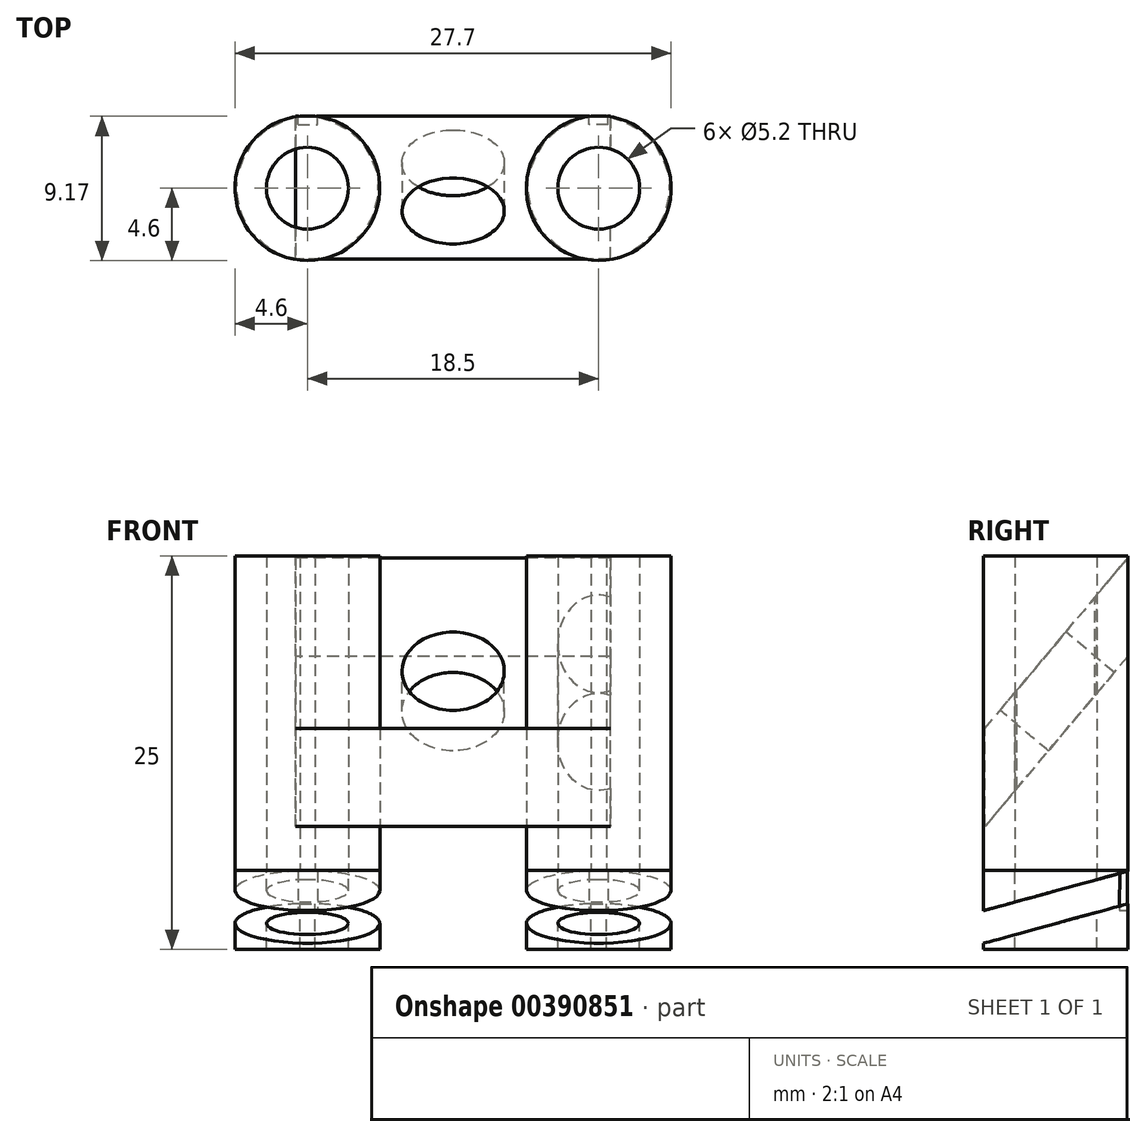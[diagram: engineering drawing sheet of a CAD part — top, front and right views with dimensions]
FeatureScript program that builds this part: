
annotation { "Feature Type Name" : "Feature", "Feature Type Description" : "" }
export const myFeature = defineFeature(function(context is Context, id is Id, definition is map)
    precondition{}
    {
        {
            var Q0;
            Q0=qCreatedBy(makeId("Top.planeOp"),FACE);
            var sketch = newSketch(context, id + "F0", { "sketchPlane" : qUnion([Q0])});
            skCircle(sketch, "E0", {"center": v(-9.25, 0) * mm, "radius": 2.6 * mm});
            skCircle(sketch, "E1", {"center": v(9.25, 0) * mm, "radius": 2.6 * mm});
            skCircle(sketch, "E2", {"center": v(-9.25, 0) * mm, "radius": 4.6 * mm});
            skCircle(sketch, "E3", {"center": v(9.25, 0) * mm, "radius": 4.6 * mm});
            skSolve(sketch);
        }
        {
            var Q0;
            Q0=makeQuery(id+"F0.imprint","IMPRINT",FACE,{"disambiguationData":[TD([[makeQuery(id+"F0.imprint","IMPRINT",EDGE,{"derivedFrom":sQuery(id+"F0.wireOp",EDGE,"E0")}),-1.0]])]});
            var Q1;
            Q1=makeQuery(id+"F0.imprint","IMPRINT",FACE,{"disambiguationData":[TD([[makeQuery(id+"F0.imprint","IMPRINT",EDGE,{"derivedFrom":sQuery(id+"F0.wireOp",EDGE,"E1")}),-1.0]])]});
            extrude(context, id + "F1", {"entities" : qUnion([Q0, Q1]), "depth" : 20 * mm, "offsetDistance" : 25 * mm});
        }
        {
            var Q0;
            Q0=qCreatedBy(makeId("Right.planeOp"),FACE);
            var sketch = newSketch(context, id + "F2", { "sketchPlane" : qUnion([Q0])});
            skLineSegment(sketch, "E4", {"start": v(-4.55, 19.95) * mm, "end": v(4.63, 9) * mm, "construction": true});
            skLineSegment(sketch, "E5", {"start": v(4.63, 9) * mm, "end": v(-4.53, 9) * mm, "construction": true});
            skLineSegment(sketch, "E6", {"start": v(-4.5, 9.04) * mm, "end": v(1.41, 16.08) * mm, "construction": true});
            skPoint(sketch, "E7.startSnap0", {"position": v(-0.12, 13.68) * mm});
            skLineSegment(sketch, "E8", {"start": v(-1.44, 6.47) * mm, "end": v(4.56, 13.61) * mm});
            skLineSegment(sketch, "E9", {"start": v(-4.5, 9.04) * mm, "end": v(-4.46, 9) * mm});
            skPoint(sketch, "E10.orphan", {"position": v(-1.24, 6.7) * mm});
            skPoint(sketch, "E11.orphan", {"position": v(-6.57, 6.58) * mm});
            skPoint(sketch, "E12.orphan", {"position": v(4.1, 13.08) * mm});
            skLineSegment(sketch, "E13.trimOffspring", {"start": v(1.41, 16.08) * mm, "end": v(-4.5, 9.04) * mm});
            skPoint(sketch, "E14.trimOffspring.end.orphan", {"position": v(4.3, 18.36) * mm});
            skLineSegment(sketch, "E15", {"start": v(1.41, 16.08) * mm, "end": v(4.56, 19.84) * mm});
            skLineSegment(sketch, "E16", {"start": v(4.56, 19.84) * mm, "end": v(4.56, 13.61) * mm});
            skLineSegment(sketch, "E17", {"start": v(-1.44, 6.47) * mm, "end": v(-4.5, 2.81) * mm});
            skLineSegment(sketch, "E18", {"start": v(-4.5, 2.81) * mm, "end": v(-4.5, 9.04) * mm});
            skSolve(sketch);
        }
        {
            var Q0;
            Q0 = qSketchRegion(id + "F2", true);
            extrude(context, id + "F3", {"entities" : qUnion([Q0]), "depth" : 10 * mm, "offsetDistance" : 25 * mm, "hasSecondDirection" : true, "secondDirectionOppositeDirection" : true, "secondDirectionDepth" : 10 * mm});
        }
        {
            var Q0;
            Q0=makeQuery(id+"F1.opExtrude","CAP_FACE",FACE,{"disambiguationData":[OSD([sQuery(id+"F0.wireOp",EDGE,"E1"),sQuery(id+"F0.wireOp",EDGE,"E3")])],"isStart":false});
            var sketch = newSketch(context, id + "F4", { "sketchPlane" : qUnion([Q0])});
            skCircle(sketch, "E19", {"center": v(9.25, 0) * mm, "radius": 2.6 * mm});
            skCircle(sketch, "E20.MirrorC", {"center": v(-9.25, 0) * mm, "radius": 2.6 * mm});
            skSolve(sketch);
        }
        {
            var Q0;
            Q0=makeQuery(id+"F4.imprint","IMPRINT",FACE,{"disambiguationData":[TD([[makeQuery(id+"F4.imprint","IMPRINT",EDGE,{"derivedFrom":sQuery(id+"F4.wireOp",EDGE,"E20.MirrorC")}),-1.0]])]});
            var Q1;
            Q1=makeQuery(id+"F4.imprint","IMPRINT",FACE,{"disambiguationData":[TD([[makeQuery(id+"F4.imprint","IMPRINT",EDGE,{"derivedFrom":sQuery(id+"F4.wireOp",EDGE,"E19")}),1.0]])]});
            extrude(context, id + "F5", {"entities" : qUnion([Q0, Q1]), "operationType" : NewBodyOperationType.REMOVE, "oppositeDirection" : true, "depth" : 25 * mm, "offsetDistance" : 25 * mm});
        }
        {
            var Q0;
            Q0=makeQuery(id+"F3.opExtrude","SWEPT_FACE",FACE,{"disambiguationData":[OSD([sQuery(id+"F2.wireOp",EDGE,"E13.trimOffspring"),sQuery(id+"F2.wireOp",EDGE,"E15")])]});
            var sketch = newSketch(context, id + "F6", { "sketchPlane" : qUnion([Q0])});
            skCircle(sketch, "E21", {"center": v(0, 8.77) * mm, "radius": 3.25 * mm});
            skSolve(sketch);
        }
        {
            var Q0;
            Q0 = qSketchRegion(id + "F6", true);
            extrude(context, id + "F7", {"entities" : qUnion([Q0]), "operationType" : NewBodyOperationType.REMOVE, "oppositeDirection" : true, "depth" : 25 * mm, "offsetDistance" : 25 * mm});
        }
        {
            var Q0;
            Q0=makeQuery(id+"F1.opExtrude","CAP_FACE",FACE,{"disambiguationData":[OSD([sQuery(id+"F0.wireOp",EDGE,"E0"),sQuery(id+"F0.wireOp",EDGE,"E2")])],"isStart":true});
            var Q1;
            Q1=makeQuery(id+"F1.opExtrude","CAP_FACE",FACE,{"disambiguationData":[OSD([sQuery(id+"F0.wireOp",EDGE,"E1"),sQuery(id+"F0.wireOp",EDGE,"E3")])],"isStart":true});
            extrude(context, id + "F8", {"entities" : qUnion([Q0, Q1]), "depth" : 5 * mm, "offsetDistance" : 25 * mm});
        }
        {
            var Q0;
            Q0=qCreatedBy(makeId("Right.planeOp"),FACE);
            var sketch = newSketch(context, id + "F9", { "sketchPlane" : qUnion([Q0])});
            skLineSegment(sketch, "E22", {"start": v(-5.77, -2.86) * mm, "end": v(4.7, 0) * mm});
            skLineSegment(sketch, "E23", {"start": v(4.7, 0) * mm, "end": v(5.8, -1.77) * mm});
            skLineSegment(sketch, "E24", {"start": v(-5.24, -4.8) * mm, "end": v(5.8, -1.77) * mm});
            skLineSegment(sketch, "E25", {"start": v(-5.24, -4.8) * mm, "end": v(-5.77, -2.86) * mm});
            skSolve(sketch);
        }
        {
            var Q0;
            Q0 = qSketchRegion(id + "F9", true);
            extrude(context, id + "F10", {"entities" : qUnion([Q0]), "operationType" : NewBodyOperationType.REMOVE, "depth" : 25 * mm, "offsetDistance" : 25 * mm, "hasSecondDirection" : true, "secondDirectionOppositeDirection" : true, "secondDirectionDepth" : 25 * mm});
        }
        {
            var Q0;
            Q0=makeQuery(id+"F3.opExtrude","SWEPT_FACE",FACE,{"disambiguationData":[OSD([sQuery(id+"F2.wireOp",EDGE,"E16")])]});
            var sketch = newSketch(context, id + "F11", { "sketchPlane" : qUnion([Q0])});
            skLineSegment(sketch, "E26.bottom", {"start": v(-9.86, 0) * mm, "end": v(-8.62, 0) * mm});
            skLineSegment(sketch, "E26.top", {"start": v(-9.86, -2.5) * mm, "end": v(-8.62, -2.5) * mm});
            skLineSegment(sketch, "E26.left", {"start": v(-9.86, 0) * mm, "end": v(-9.86, -2.5) * mm});
            skLineSegment(sketch, "E26.right", {"start": v(-8.62, 0) * mm, "end": v(-8.62, -2.5) * mm});
            skLineSegment(sketch, "E27.MirrorCS", {"start": v(8.62, 0) * mm, "end": v(8.62, -2.5) * mm});
            skLineSegment(sketch, "E28.MirrorCS", {"start": v(9.86, 0) * mm, "end": v(9.86, -2.5) * mm});
            skLineSegment(sketch, "E29.MirrorCS", {"start": v(9.86, 0) * mm, "end": v(8.62, 0) * mm});
            skLineSegment(sketch, "E30.MirrorCS", {"start": v(9.86, -2.5) * mm, "end": v(8.62, -2.5) * mm});
            skSolve(sketch);
        }
        {
            var Q0;
            Q0=makeQuery(id+"F11.imprint","IMPRINT",FACE,{"disambiguationData":[TD([[makeQuery(id+"F11.imprint","IMPRINT",EDGE,{"derivedFrom":sQuery(id+"F11.wireOp",EDGE,"E26.bottom")}),-1.0]])]});
            var Q1;
            Q1=makeQuery(id+"F11.imprint","IMPRINT",FACE,{"disambiguationData":[TD([[makeQuery(id+"F11.imprint","IMPRINT",EDGE,{"derivedFrom":sQuery(id+"F11.wireOp",EDGE,"E27.MirrorCS")}),1.0]])]});
            extrude(context, id + "F12", {"entities" : qUnion([Q0, Q1]), "oppositeDirection" : true, "depth" : .5 * mm, "offsetDistance" : 25 * mm});
        }
        {
            var Q0;
            Q0=makeQuery(id+"F1.opExtrude","CAP_FACE",FACE,{"disambiguationData":[OSD([sQuery(id+"F0.wireOp",EDGE,"E0"),sQuery(id+"F0.wireOp",EDGE,"E2")])],"isStart":false});
            var sketch = newSketch(context, id + "F13", { "sketchPlane" : qUnion([Q0])});
            skLineSegment(sketch, "E31.bottom", {"start": v(-10.07, 4.57) * mm, "end": v(10.74, 4.57) * mm});
            skLineSegment(sketch, "E31.top", {"start": v(-10.07, 6.32) * mm, "end": v(10.74, 6.32) * mm});
            skLineSegment(sketch, "E31.left", {"start": v(-10.07, 4.57) * mm, "end": v(-10.07, 6.32) * mm});
            skLineSegment(sketch, "E31.right", {"start": v(10.74, 4.57) * mm, "end": v(10.74, 6.32) * mm});
            skSolve(sketch);
        }
        {
            var Q0;
            Q0 = qSketchRegion(id + "F13", true);
            extrude(context, id + "F14", {"entities" : qUnion([Q0]), "operationType" : NewBodyOperationType.REMOVE, "oppositeDirection" : true, "depth" : 30 * mm, "offsetDistance" : 25 * mm});
        }
    });
